# Revit family: L-PL낙엽교목_감나무
name_source: partatom
category: 수목
units: mm (PartAtom-declared; Revit-internal decimal feet)

## family parameters
OmniClass 번호 = 23.40.05.00
OmniClass 제목 = Plants and Planting Products
공유 = 아니오
렌더 모양 소스 = 패밀리 형상
로드될 때 보이드를 사용하여 절단 = 아니오
작업 기준면 기반 = 아니오
항상 수직 = 예

## types (1)
- 감나무
    H = 5000  [stored 16.4042 ft]
    KBIMS_보급정보-저작자 = 림인포테크_MMJ
    LIM_INFO_PL_M2당수량 = 0
    LIM_INFO_PL_가격 = 0 $
    LIM_INFO_PL_구분 = 상록교목
    LIM_INFO_PL_규격 = 5.0H X 18R
    LIM_INFO_PL_수목단위 = 주
    LIM_INFO_PL_주당인정수량 = 0
    LIM_INFO_PL_품명 = 가시나무
    LIM_INFO_PL_학명 = Quercus myrsinaefolia Bl.
    LIM_INFO_버전 = 2022_V01
    LIM_INFO_제작일 = 20211210
    LIM_INFO_주의사항 = 재배포, 재가공, 판매 금지
    R = 200  [stored 0.656168 ft]
    건설정보분류체계-부위분류 = E985
    높이 = 5000  [stored 16.4042 ft]
    뿌리분 높이 = 545
    뿌리분 직경 = 1090
    조달청표준공사코드-세부공종 = 10161599202809
    콘 높이 = 273

note: [stored X ft] marks values corroborated as IEEE doubles in the binary element streams (Revit-internal decimal feet)
